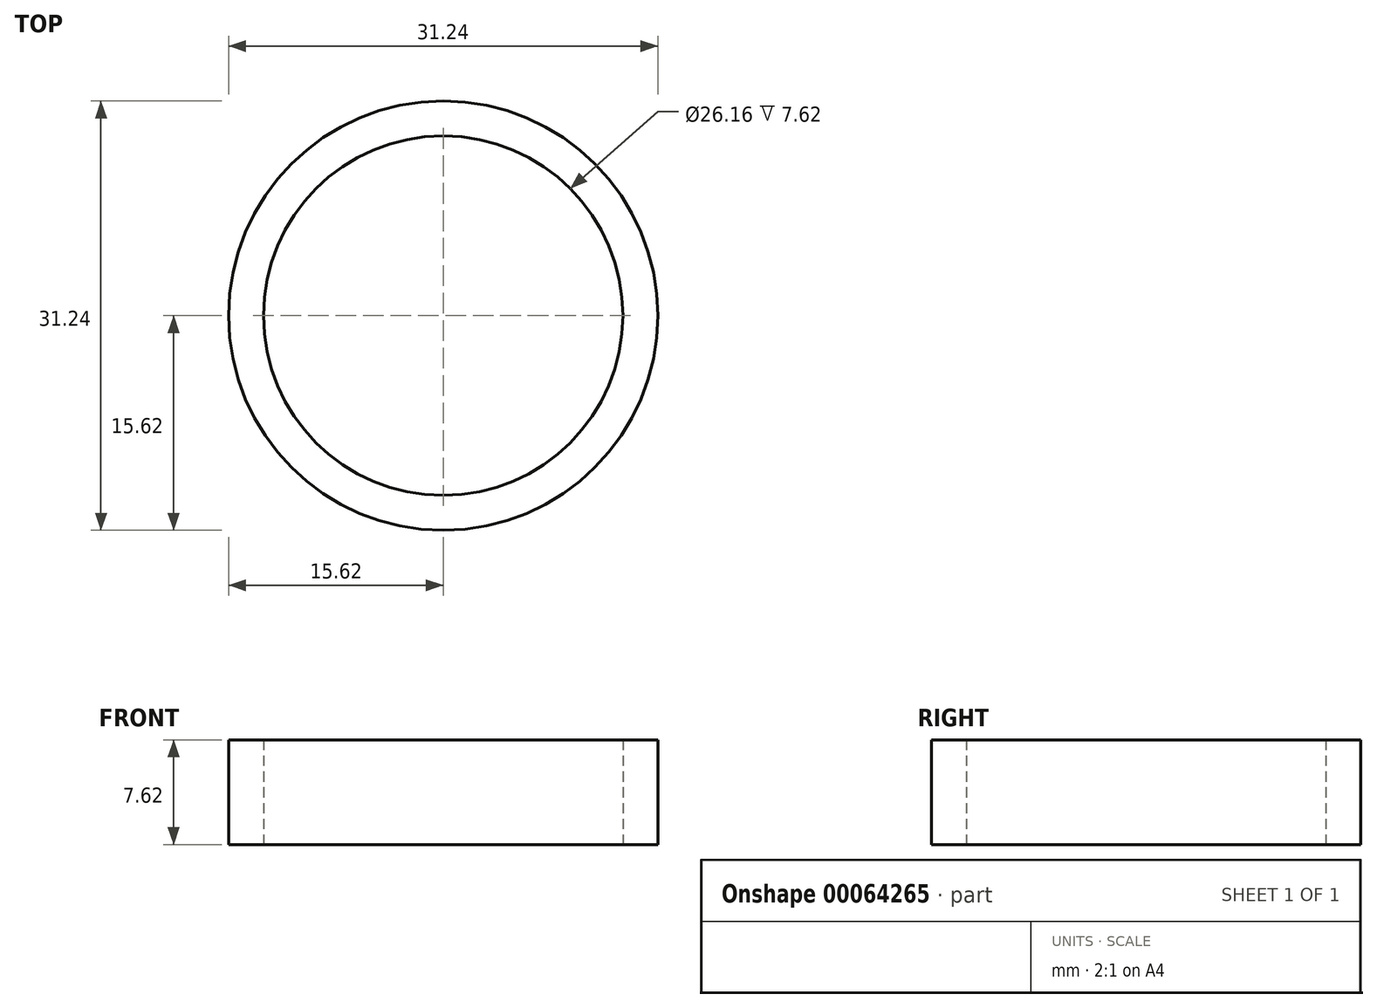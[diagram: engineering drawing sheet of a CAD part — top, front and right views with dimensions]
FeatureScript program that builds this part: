
annotation { "Feature Type Name" : "Feature", "Feature Type Description" : "" }
export const myFeature = defineFeature(function(context is Context, id is Id, definition is map)
    precondition{}
    {
        {
            var Q0;
            Q0=qCreatedBy(makeId("Top.planeOp"),FACE);
            var sketch = newSketch(context, id + "F0", { "sketchPlane" : qUnion([Q0])});
            skCircle(sketch, "E0", {"center": v(0, 0) * mm, "radius": 13.08 * mm});
            skCircle(sketch, "E1", {"center": v(0, 0) * mm, "radius": 15.62 * mm});
            skSolve(sketch);
        }
        {
            var Q0;
            Q0 = qSketchRegion(id + "F0", true);
            extrude(context, id + "F1", {"entities" : qUnion([Q0]), "depth" : 7.62 * mm, "offsetDistance" : 25.4 * mm});
        }
    });
